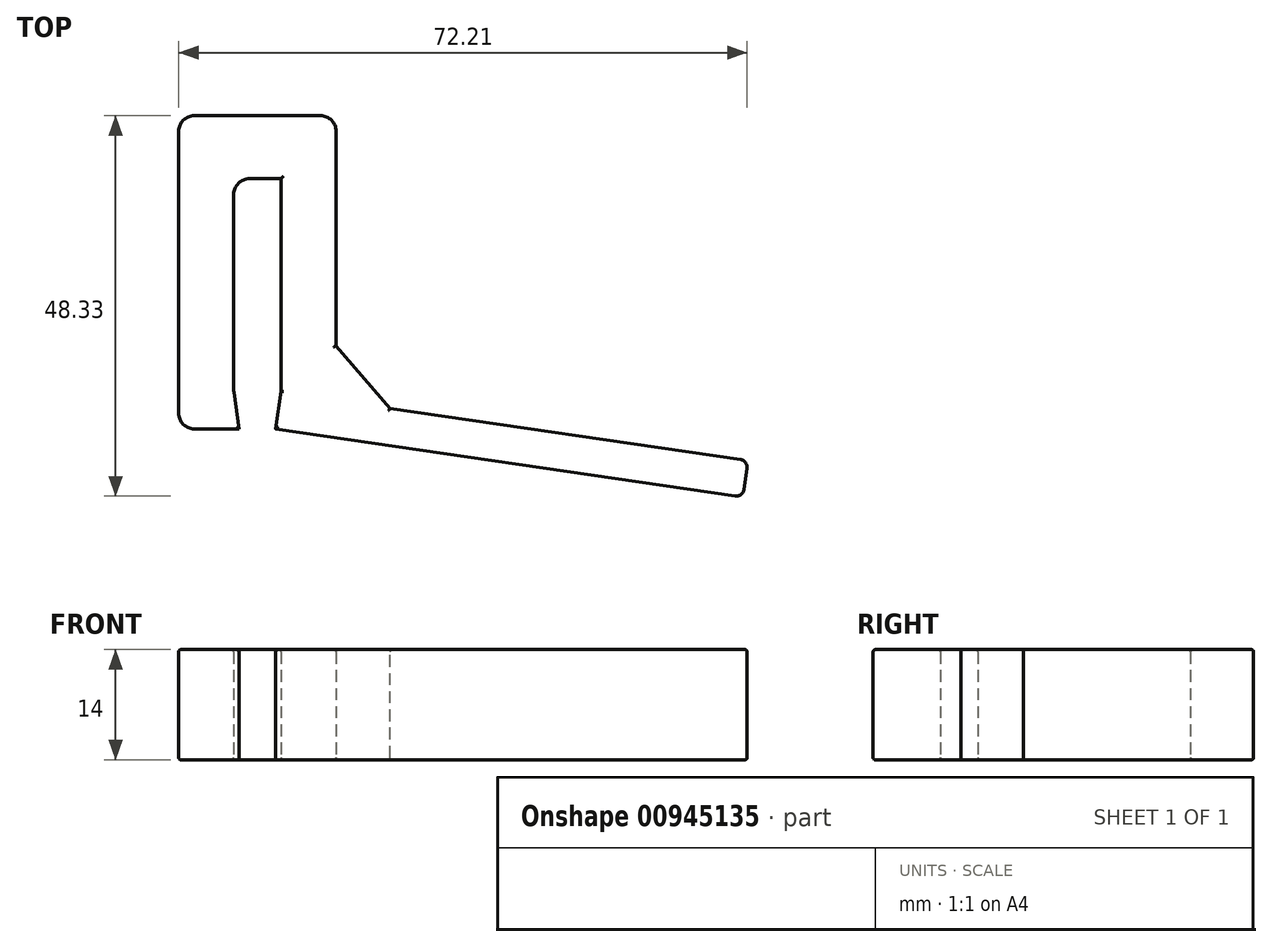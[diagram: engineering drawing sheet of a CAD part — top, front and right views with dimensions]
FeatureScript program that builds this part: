
annotation { "Feature Type Name" : "Feature", "Feature Type Description" : "" }
export const myFeature = defineFeature(function(context is Context, id is Id, definition is map)
    precondition{}
    {
        {
            var Q0;
            Q0=qCreatedBy(makeId("Top.planeOp"),FACE);
            var sketch = newSketch(context, id + "F0", { "sketchPlane" : qUnion([Q0])});
            skLineSegment(sketch, "E0.left", {"start": v(0, 0) * mm, "end": v(0, 27) * mm});
            skLineSegment(sketch, "E0.right", {"start": v(-6, 0) * mm, "end": v(-6, 27) * mm});
            skLineSegment(sketch, "E1.right", {"start": v(0, 27) * mm, "end": v(0, 0) * mm});
            skLineSegment(sketch, "E2", {"start": v(-6, 27) * mm, "end": v(0, 27) * mm});
            skLineSegment(sketch, "E3", {"start": v(7, 35) * mm, "end": v(7, -4.79) * mm});
            skLineSegment(sketch, "E4", {"start": v(-13, -4.79) * mm, "end": v(-5.3, -4.79) * mm});
            skLineSegment(sketch, "E5", {"start": v(-5.3, -4.79) * mm, "end": v(-6, 0) * mm});
            skLineSegment(sketch, "E6", {"start": v(7, -4.79) * mm, "end": v(-0.7, -4.79) * mm});
            skLineSegment(sketch, "E7", {"start": v(-0.7, -4.79) * mm, "end": v(0, 0) * mm});
            skLineSegment(sketch, "E8", {"start": v(7, 35) * mm, "end": v(-13, 35) * mm});
            skLineSegment(sketch, "E9", {"start": v(-13, 35) * mm, "end": v(-13, -4.79) * mm});
            skSolve(sketch);
        }
        {
            var Q0;
            Q0=makeQuery(id+"F0.imprint","IMPRINT",FACE,{"disambiguationData":[TD([[makeQuery(id+"F0.imprint","IMPRINT",EDGE,{"derivedFrom":sQuery(id+"F0.wireOp",EDGE,"E0.right")}),1.0]])]});
            var Q1;
            Q1 = qSketchRegion(id + "FrMtNXytxQ7akZ8_1", true);
            extrude(context, id + "F1", {"entities" : qUnion([Q0, Q1]), "depth" : 14 * mm, "offsetDistance" : 25 * mm});
        }
        {
            var Q0;
            Q0=makeQuery(id+"F1.opExtrude","SWEPT_EDGE",EDGE,{"disambiguationData":[OSD([sQuery(id+"F0.wireOp",EDGE,"PczdBa6P-nFhw-pfaQ-qJhu-VVp3lQY8YuxU.bottom"),sQuery(id+"F0.wireOp",EDGE,"PczdBa6P-nFhw-pfaQ-qJhu-VVp3lQY8YuxU.left")])]});
            var Q1;
            Q1=makeQuery(id+"F1.opExtrude","SWEPT_EDGE",EDGE,{"disambiguationData":[OSD([sQuery(id+"F0.wireOp",EDGE,"PczdBa6P-nFhw-pfaQ-qJhu-VVp3lQY8YuxU.bottom"),sQuery(id+"F0.wireOp",EDGE,"E3")])]});
            var Q2;
            Q2=makeQuery(id+"F1.opExtrude","SWEPT_EDGE",EDGE,{"disambiguationData":[OSD([sQuery(id+"F0.wireOp",EDGE,"E3"),sQuery(id+"F0.wireOp",EDGE,"aoy2P97I-7hsh-VHDM-M3ku-ahT5R2Tx9LTX")])]});
            var Q3;
            Q3=makeQuery(id+"F1.opExtrude","SWEPT_EDGE",EDGE,{"disambiguationData":[OSD([sQuery(id+"F0.wireOp",EDGE,"E1.right"),sQuery(id+"F0.wireOp",EDGE,"aoy2P97I-7hsh-VHDM-M3ku-ahT5R2Tx9LTX")])]});
            var Q4;
            Q4=makeQuery(id+"F1.opExtrude","SWEPT_EDGE",EDGE,{"disambiguationData":[OSD([sQuery(id+"F0.wireOp",EDGE,"E0.right"),sQuery(id+"F0.wireOp",EDGE,"PczdBa6P-nFhw-pfaQ-qJhu-VVp3lQY8YuxU.top")])]});
            var Q5;
            Q5=makeQuery(id+"F1.opExtrude","SWEPT_EDGE",EDGE,{"disambiguationData":[OSD([sQuery(id+"F0.wireOp",EDGE,"PczdBa6P-nFhw-pfaQ-qJhu-VVp3lQY8YuxU.top"),sQuery(id+"F0.wireOp",EDGE,"PczdBa6P-nFhw-pfaQ-qJhu-VVp3lQY8YuxU.left")])]});
            var Q6;
            Q6=makeQuery(id+"F1.opExtrude","SWEPT_EDGE",EDGE,{"disambiguationData":[OSD([sQuery(id+"F0.wireOp",EDGE,"E8"),sQuery(id+"F0.wireOp",EDGE,"E9")])]});
            var Q7;
            Q7=makeQuery(id+"F1.opExtrude","SWEPT_EDGE",EDGE,{"disambiguationData":[OSD([sQuery(id+"F0.wireOp",EDGE,"E4"),sQuery(id+"F0.wireOp",EDGE,"E9")])]});
            fillet(context, id + "F2", {"entities" : qUnion([Q0, Q1, Q2, Q3, Q4, Q5, Q6, Q7]), "radius" : 2 * mm, "tangentPropagation" : true, "allowEdgeOverflow" : false});
        }
        {
            var Q0;
            Q0=makeQuery(id+"F1.opExtrude","SWEPT_FACE",FACE,{"disambiguationData":[OSD([sQuery(id+"F0.wireOp",EDGE,"E7")])]});
            var sketch = newSketch(context, id + "F3", { "sketchPlane" : qUnion([Q0])});
            skLineSegment(sketch, "E10.bottom", {"start": v(4.84, 14) * mm, "end": v(0.15, 14) * mm});
            skLineSegment(sketch, "E10.top", {"start": v(4.84, 0) * mm, "end": v(0.15, 0) * mm});
            skLineSegment(sketch, "E10.left", {"start": v(4.84, 14) * mm, "end": v(4.84, 0) * mm});
            skLineSegment(sketch, "E10.right", {"start": v(0.15, 14) * mm, "end": v(0.15, 0) * mm});
            skSolve(sketch);
        }
        {
            var Q0;
            Q0 = qSketchRegion(id + "F3", true);
            extrude(context, id + "F4", {"entities" : qUnion([Q0]), "operationType" : NewBodyOperationType.ADD, "oppositeDirection" : true, "depth" : 60 * mm, "offsetDistance" : 25 * mm});
        }
        {
            var Q0;
            Q0=makeQuery(id+"F4.boolean.opBoolean","INTERSECT",EDGE,{"derivedFrom":[makeQuery(id+"F1.opExtrude","SWEPT_FACE",FACE,{"disambiguationData":[OSD([sQuery(id+"F0.wireOp",EDGE,"E3")])]}),makeQuery(id+"F4.opExtrude","SWEPT_FACE",FACE,{"disambiguationData":[OSD([sQuery(id+"F3.wireOp",EDGE,"E10.right")])]})]});
            chamfer(context, id + "F5", {"entities" : qUnion([Q0]), "width" : 8 * mm, "tangentPropagation" : true});
        }
        {
            var Q0;
            Q0=makeQuery(id+"F4.boolean.opBoolean","MERGE",FACE,{"derivedFrom":[makeQuery(id+"F1.opExtrude","CAP_FACE",FACE,{"disambiguationData":[OSD([sQuery(id+"F0.wireOp",EDGE,"E0.right"),sQuery(id+"F0.wireOp",EDGE,"E1.right"),sQuery(id+"F0.wireOp",EDGE,"E2"),sQuery(id+"F0.wireOp",EDGE,"E3"),sQuery(id+"F0.wireOp",EDGE,"E4"),sQuery(id+"F0.wireOp",EDGE,"E5"),sQuery(id+"F0.wireOp",EDGE,"E6"),sQuery(id+"F0.wireOp",EDGE,"E7"),sQuery(id+"F0.wireOp",EDGE,"E8"),sQuery(id+"F0.wireOp",EDGE,"E9")])],"isStart":false}),makeQuery(id+"F4.opExtrude","SWEPT_FACE",FACE,{"disambiguationData":[OSD([sQuery(id+"F3.wireOp",EDGE,"E10.bottom")])]})]});
            var Q1;
            Q1=makeQuery(id+"F4.boolean.opBoolean","MERGE",FACE,{"derivedFrom":[makeQuery(id+"F1.opExtrude","CAP_FACE",FACE,{"disambiguationData":[OSD([sQuery(id+"F0.wireOp",EDGE,"E0.right"),sQuery(id+"F0.wireOp",EDGE,"E1.right"),sQuery(id+"F0.wireOp",EDGE,"E2"),sQuery(id+"F0.wireOp",EDGE,"E3"),sQuery(id+"F0.wireOp",EDGE,"E4"),sQuery(id+"F0.wireOp",EDGE,"E5"),sQuery(id+"F0.wireOp",EDGE,"E6"),sQuery(id+"F0.wireOp",EDGE,"E7"),sQuery(id+"F0.wireOp",EDGE,"E8"),sQuery(id+"F0.wireOp",EDGE,"E9")])],"isStart":true}),makeQuery(id+"F4.opExtrude","SWEPT_FACE",FACE,{"disambiguationData":[OSD([sQuery(id+"F3.wireOp",EDGE,"E10.top")])]})]});
            fillet(context, id + "F6", {"entities" : qUnion([Q0, Q1]), "radius" : .3 * mm, "tangentPropagation" : true, "allowEdgeOverflow" : false});
        }
        {
            var Q0;
            Q0=makeQuery(id+"F4.opExtrude","CAP_EDGE",EDGE,{"disambiguationData":[OSD([sQuery(id+"F3.wireOp",EDGE,"E10.right")])],"isStart":false});
            var Q1;
            Q1=makeQuery(id+"F4.opExtrude","CAP_EDGE",EDGE,{"disambiguationData":[OSD([sQuery(id+"F3.wireOp",EDGE,"E10.left")])],"isStart":false});
            fillet(context, id + "F7", {"entities" : qUnion([Q0, Q1]), "radius" : 1 * mm, "tangentPropagation" : true, "allowEdgeOverflow" : false});
        }
    });
